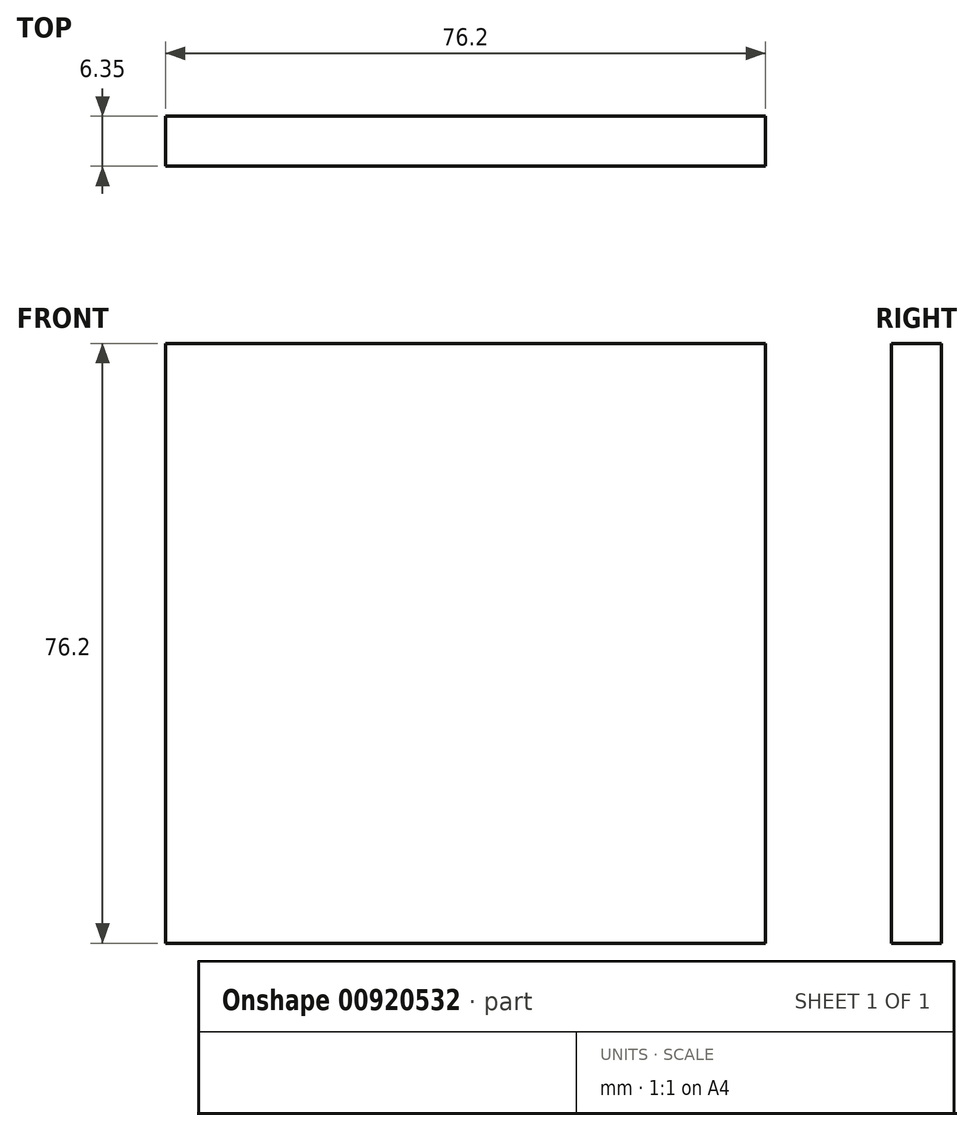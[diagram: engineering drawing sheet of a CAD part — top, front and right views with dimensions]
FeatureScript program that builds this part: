
annotation { "Feature Type Name" : "Feature", "Feature Type Description" : "" }
export const myFeature = defineFeature(function(context is Context, id is Id, definition is map)
    precondition{}
    {
        {
            var Q0;
            Q0=qCreatedBy(makeId("Front.planeOp"),FACE);
            var sketch = newSketch(context, id + "F0", { "sketchPlane" : qUnion([Q0])});
            skLineSegment(sketch, "E0.bottom", {"start": v(0, 38.1) * mm, "end": v(76.2, 38.1) * mm});
            skLineSegment(sketch, "E0.top", {"start": v(0, -38.1) * mm, "end": v(76.2, -38.1) * mm});
            skLineSegment(sketch, "E0.left", {"start": v(0, 38.1) * mm, "end": v(0, -38.1) * mm});
            skLineSegment(sketch, "E0.right", {"start": v(76.2, 38.1) * mm, "end": v(76.2, -38.1) * mm});
            skSolve(sketch);
        }
        {
            var Q0;
            Q0=makeQuery(id+"F0.imprint","IMPRINT",FACE,{"disambiguationData":[TD([[makeQuery(id+"F0.imprint","IMPRINT",EDGE,{"derivedFrom":sQuery(id+"F0.wireOp",EDGE,"E0.bottom")}),-1.0]])]});
            extrude(context, id + "F1", {"entities" : qUnion([Q0]), "oppositeDirection" : true, "depth" : 6.35 * mm, "offsetDistance" : 25.4 * mm});
        }
    });
